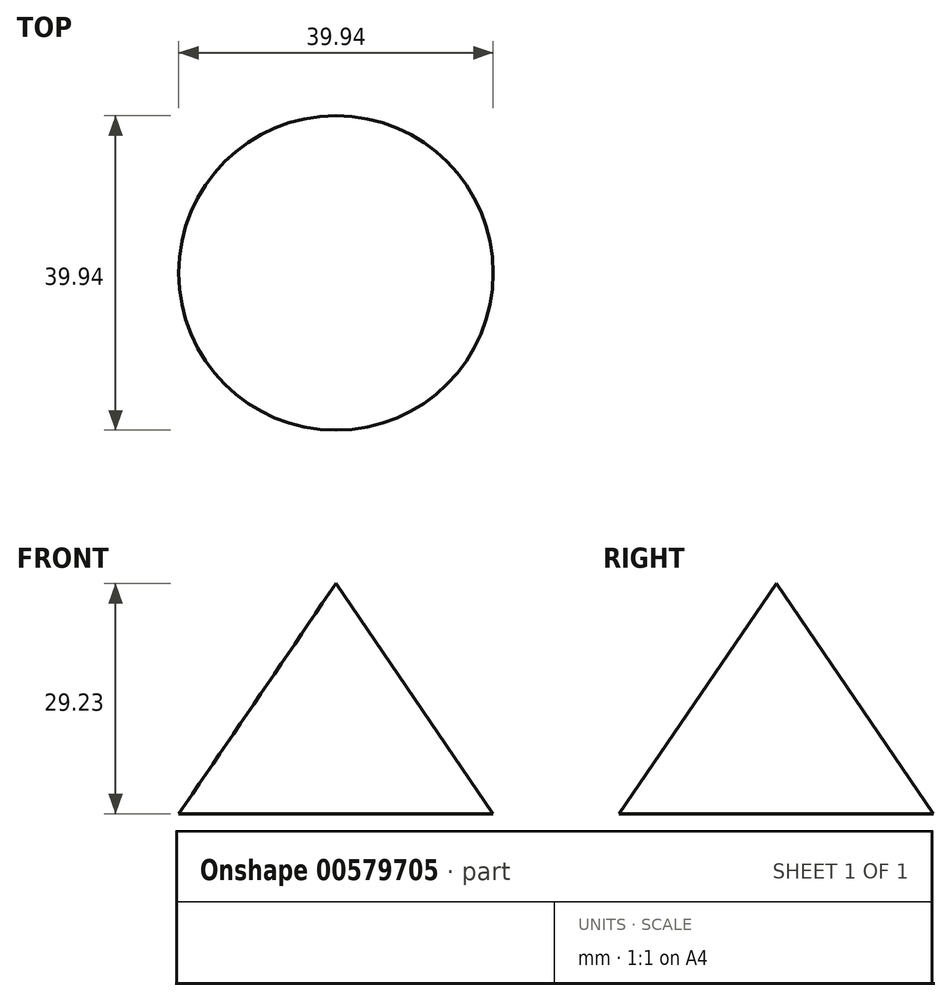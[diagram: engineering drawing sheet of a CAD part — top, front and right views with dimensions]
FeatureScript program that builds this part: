
annotation { "Feature Type Name" : "Feature", "Feature Type Description" : "" }
export const myFeature = defineFeature(function(context is Context, id is Id, definition is map)
    precondition{}
    {
        {
            var Q0;
            Q0=qCreatedBy(makeId("Front.planeOp"),FACE);
            var sketch = newSketch(context, id + "F0", { "sketchPlane" : qUnion([Q0])});
            skLineSegment(sketch, "E0", {"start": v(0, 0) * mm, "end": v(0, 29.23) * mm});
            skLineSegment(sketch, "E1", {"start": v(0, 29.23) * mm, "end": v(19.97, 0) * mm});
            skLineSegment(sketch, "E2", {"start": v(19.97, 0) * mm, "end": v(0, 0) * mm});
            skSolve(sketch);
        }
        {
            var Q0;
            Q0 = qSketchRegion(id + "F0", true);
            var Q1;
            Q1=sQuery(id+"F0.wireOp",EDGE,"E0");
            revolve(context, id + "F1", {"entities" : qUnion([Q0]), "axis" : qUnion([Q1]), "revolveType" : RevolveType.FULL});
        }
    });
